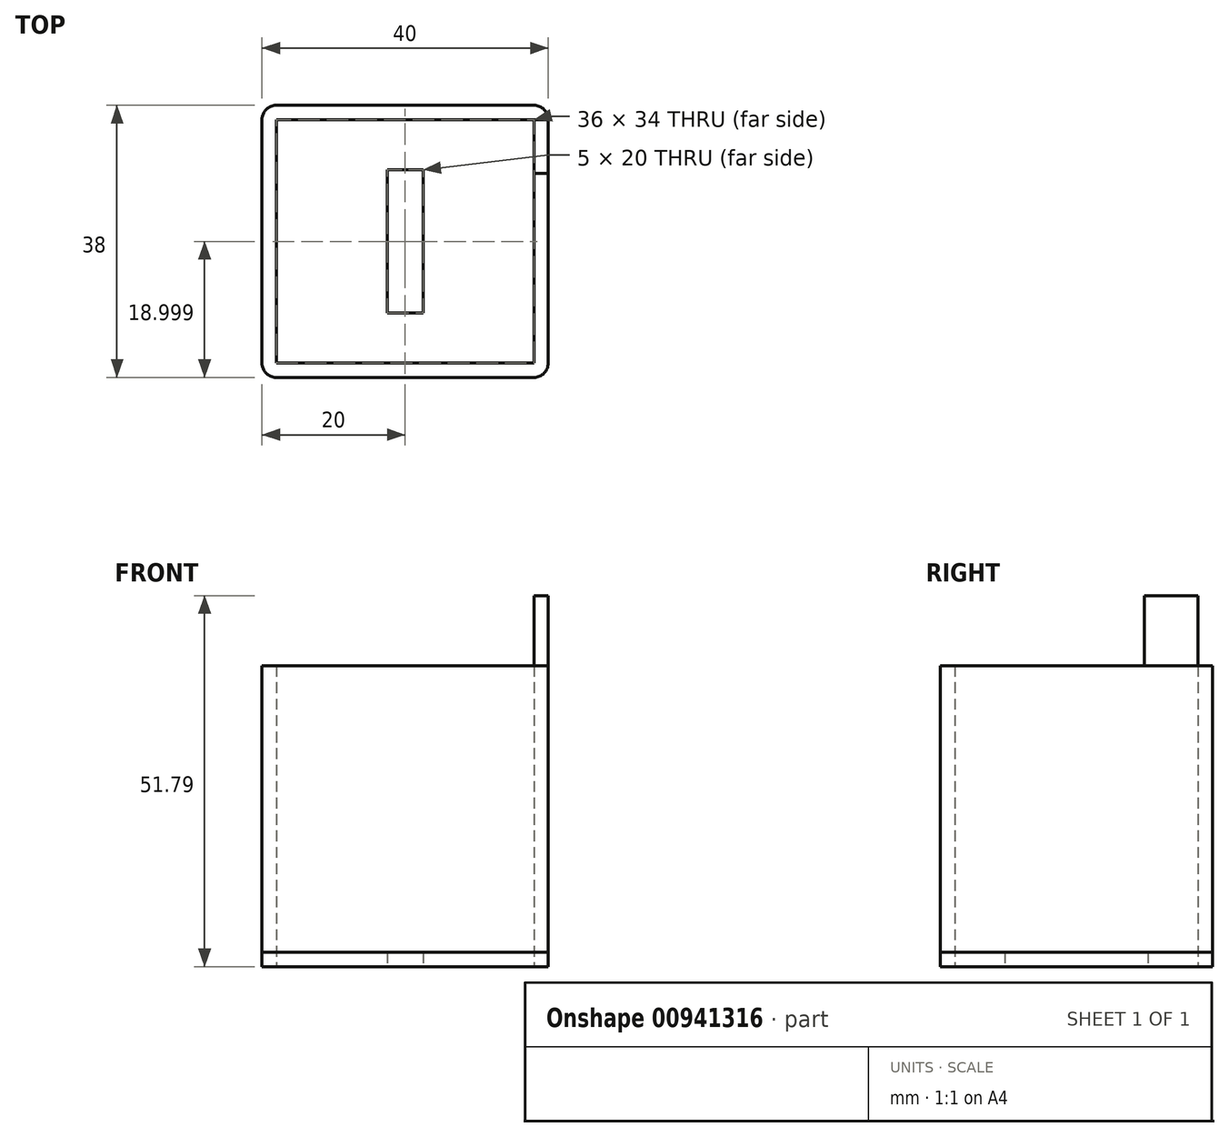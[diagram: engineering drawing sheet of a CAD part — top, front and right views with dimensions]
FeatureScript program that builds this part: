
annotation { "Feature Type Name" : "Feature", "Feature Type Description" : "" }
export const myFeature = defineFeature(function(context is Context, id is Id, definition is map)
    precondition{}
    {
        {
            var Q0;
            Q0=qCreatedBy(makeId("Top.planeOp"),FACE);
            var sketch = newSketch(context, id + "F0", { "sketchPlane" : qUnion([Q0])});
            skLineSegment(sketch, "E0.bottom", {"start": v(-18, 17.17) * mm, "end": v(18, 17.17) * mm});
            skLineSegment(sketch, "E0.top", {"start": v(-18, -16.83) * mm, "end": v(18, -16.83) * mm});
            skLineSegment(sketch, "E0.left", {"start": v(-18, 17.17) * mm, "end": v(-18, -16.83) * mm});
            skLineSegment(sketch, "E0.right", {"start": v(18, 17.17) * mm, "end": v(18, -16.83) * mm});
            skLineSegment(sketch, "E1.0", {"start": v(20, 17.17) * mm, "end": v(20, -16.83) * mm});
            skLineSegment(sketch, "E1.1", {"start": v(-18, 19.17) * mm, "end": v(18, 19.17) * mm});
            skLineSegment(sketch, "E1.2", {"start": v(-20, 17.17) * mm, "end": v(-20, -16.83) * mm});
            skLineSegment(sketch, "E1.3", {"start": v(-18, -18.83) * mm, "end": v(18, -18.83) * mm});
            skPoint(sketch, "E2.visualSharp", {"position": v(-20, -18.83) * mm});
            skArc(sketch, "E2.filletArc", {"start": v(-20, -16.83) * mm, "mid": v(-19.41, -18.25) * mm, "end": v(-18, -18.83) * mm});
            skPoint(sketch, "E3.visualSharp", {"position": v(-20, 19.17) * mm});
            skArc(sketch, "E3.filletArc", {"start": v(-18, 19.17) * mm, "mid": v(-19.41, 18.58) * mm, "end": v(-20, 17.17) * mm});
            skPoint(sketch, "E4.visualSharp", {"position": v(20, 19.17) * mm});
            skArc(sketch, "E4.filletArc", {"start": v(20, 17.17) * mm, "mid": v(19.41, 18.58) * mm, "end": v(18, 19.17) * mm});
            skPoint(sketch, "E5.visualSharp", {"position": v(20, -18.83) * mm});
            skArc(sketch, "E5.filletArc", {"start": v(18, -18.83) * mm, "mid": v(19.41, -18.25) * mm, "end": v(20, -16.83) * mm});
            skLineSegment(sketch, "E6.bottom", {"start": v(-2.5, -9.83) * mm, "end": v(2.5, -9.83) * mm});
            skLineSegment(sketch, "E6.top", {"start": v(-2.5, 10.17) * mm, "end": v(2.5, 10.17) * mm});
            skLineSegment(sketch, "E6.left", {"start": v(-2.5, -9.83) * mm, "end": v(-2.5, 10.17) * mm});
            skLineSegment(sketch, "E6.right", {"start": v(2.5, -9.83) * mm, "end": v(2.5, 10.17) * mm});
            skLineSegment(sketch, "E7", {"start": v(-18, 8.88) * mm, "end": v(-2.5, 8.88) * mm, "construction": true});
            skLineSegment(sketch, "E8", {"start": v(2.5, 2.27) * mm, "end": v(18, 2.27) * mm, "construction": true});
            skLineSegment(sketch, "E9", {"start": v(0, 10.17) * mm, "end": v(0, 17.17) * mm, "construction": true});
            skLineSegment(sketch, "E10", {"start": v(2.83, -9.83) * mm, "end": v(2.83, -16.83) * mm, "construction": true});
            skSolve(sketch);
        }
        {
            var Q0;
            Q0=qSketchRegion(id+"F0",true);
            var Q1;
            Q1=makeQuery(id+"F0.imprint","IMPRINT",FACE,{"disambiguationData":[TD([[makeQuery(id+"F0.imprint","IMPRINT",EDGE,{"derivedFrom":sQuery(id+"F0.wireOp",EDGE,"E0.bottom")}),-1.0]])]});
            extrude(context, id + "F1", {"entities" : qUnion([Q0, Q1]), "depth" : 2 * mm, "offsetDistance" : 25 * mm});
        }
        {
            var Q0;
            Q0=qSketchRegion(id+"F0",true);
            extrude(context, id + "F2", {"entities" : qUnion([Q0]), "depth" : 42 * mm, "offsetDistance" : 25 * mm});
        }
        {
            var Q0;
            Q0=makeQuery(id+"F2.opExtrude","SWEPT_FACE",FACE,{"disambiguationData":[OSD([sQuery(id+"F0.wireOp",EDGE,"E1.0")])]});
            var sketch = newSketch(context, id + "F3", { "sketchPlane" : qUnion([Q0])});
            skLineSegment(sketch, "E11", {"start": v(17.17, 42) * mm, "end": v(17.17, 51.79) * mm});
            skLineSegment(sketch, "E12", {"start": v(9.67, 51.79) * mm, "end": v(17.17, 51.79) * mm});
            skLineSegment(sketch, "E13", {"start": v(9.67, 51.79) * mm, "end": v(9.67, 42) * mm});
            skSolve(sketch);
        }
        {
            var Q0;
            {var subQ0=sQuery(id+"F3.wireOp",EDGE,"E11");Q0=makeQuery(id+"F3.imprint","IMPRINT",FACE,{"disambiguationData":[TD([[makeQuery(id+"F3.imprint","IMPRINT",EDGE,{"derivedFrom":subQ0}),1.0]])]});}
            extrude(context, id + "F4", {"entities" : qUnion([Q0]), "depth" : -2 * mm, "offsetDistance" : 25 * mm});
        }
    });
